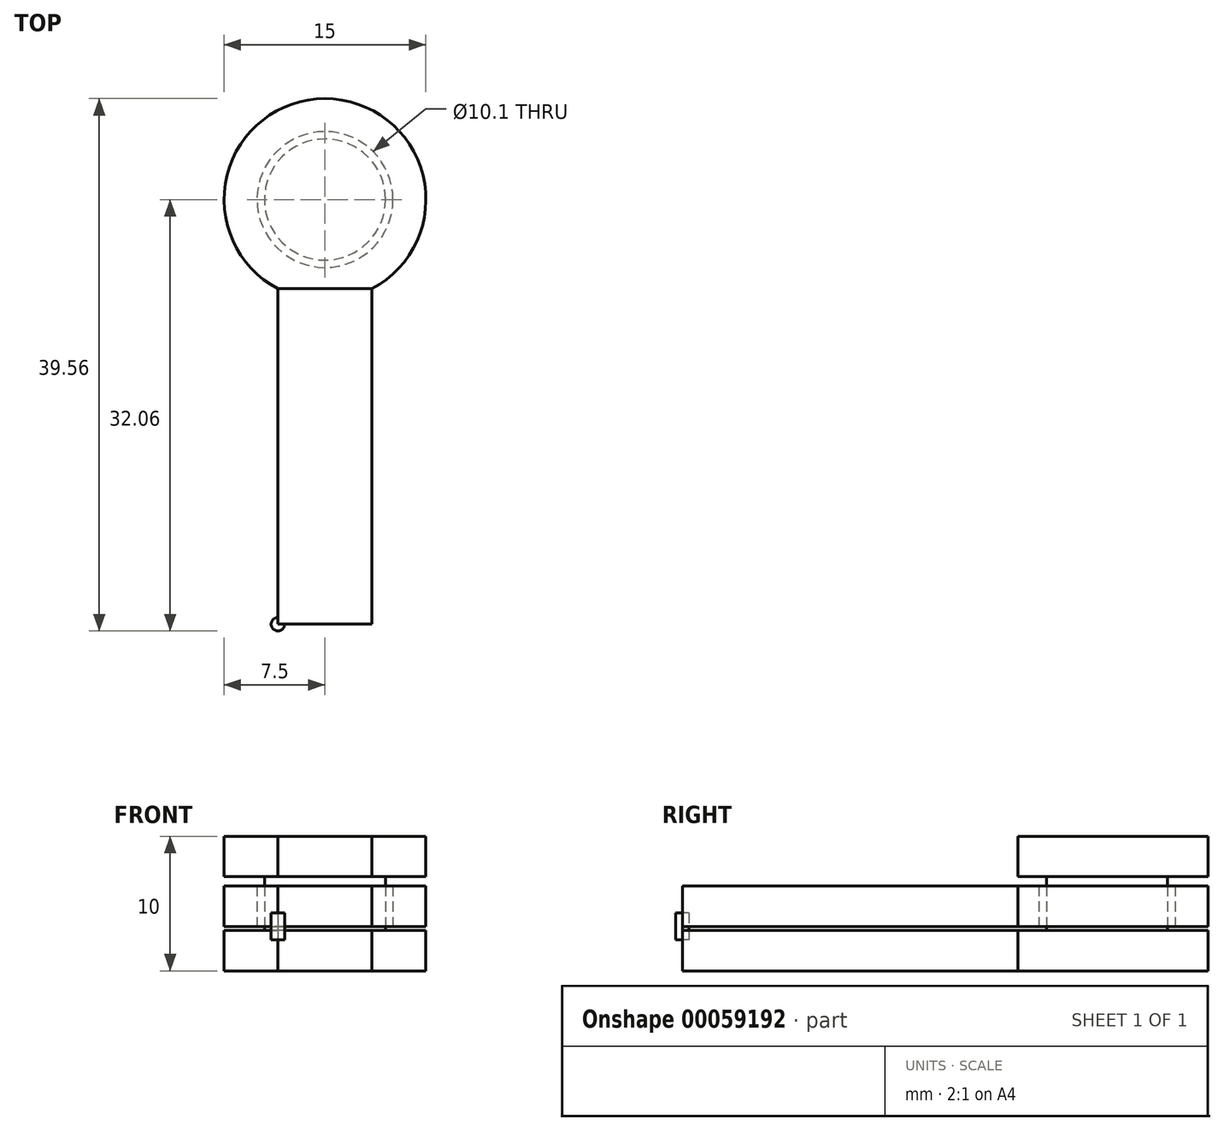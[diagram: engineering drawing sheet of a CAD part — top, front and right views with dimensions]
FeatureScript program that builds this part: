
annotation { "Feature Type Name" : "Feature", "Feature Type Description" : "" }
export const myFeature = defineFeature(function(context is Context, id is Id, definition is map)
    precondition{}
    {
        {
            var Q0;
            Q0=qCreatedBy(makeId("Top.planeOp"),FACE);
            var sketch = newSketch(context, id + "F0", { "sketchPlane" : qUnion([Q0])});
            skCircle(sketch, "E0", {"center": v(0, 0) * mm, "radius": 4.5 * mm});
            skArc(sketch, "E1", {"start": v(3.5, -6.63) * mm, "mid": v(0, 7.5) * mm, "end": v(-3.5, -6.63) * mm});
            skLineSegment(sketch, "E2.rect.bottom", {"start": v(3.5, -31.56) * mm, "end": v(-3.5, -31.56) * mm});
            skLineSegment(sketch, "E2.rect.top", {"start": v(3.5, -5.52) * mm, "end": v(-3.5, -5.52) * mm});
            skLineSegment(sketch, "E2.rect.left", {"start": v(3.5, -31.56) * mm, "end": v(3.5, -5.52) * mm});
            skLineSegment(sketch, "E2.rect.right", {"start": v(-3.5, -31.56) * mm, "end": v(-3.5, -5.52) * mm});
            skPoint(sketch, "E2.rect.middle", {"position": v(0, -18.54) * mm});
            skSolve(sketch);
        }
        {
            var Q0;
            Q0=qCreatedBy(makeId("Top.planeOp"),FACE);
            cPlane(context, id + "F1", {"entities" : qUnion([Q0]), "cplaneType" : CPlaneType.OFFSET, "offset" : 3.3 * mm, "width" : 150 * mm, "height" : 150 * mm});
        }
        {
            var Q0;
            Q0=qCreatedBy(id+"F1.planeOp",FACE);
            var sketch = newSketch(context, id + "F2", { "sketchPlane" : qUnion([Q0])});
            skLineSegment(sketch, "E3.0.0", {"start": v(3.5, -5.52) * mm, "end": v(3.5, -6.63) * mm});
            skArc(sketch, "E3.0.1", {"start": v(3.5, -6.63) * mm, "mid": v(0, 7.5) * mm, "end": v(-3.5, -6.63) * mm});
            skLineSegment(sketch, "E3.0.2", {"start": v(-3.5, -6.63) * mm, "end": v(-3.5, -5.52) * mm});
            skLineSegment(sketch, "E3.0.3", {"start": v(-3.5, -5.52) * mm, "end": v(3.5, -5.52) * mm});
            skLineSegment(sketch, "E4.0.0", {"start": v(-3.5, -31.56) * mm, "end": v(3.5, -31.56) * mm});
            skLineSegment(sketch, "E4.0.1", {"start": v(3.5, -31.56) * mm, "end": v(3.5, -6.63) * mm});
            skLineSegment(sketch, "E4.0.2", {"start": v(3.5, -6.63) * mm, "end": v(3.5, -5.52) * mm});
            skLineSegment(sketch, "E4.0.3", {"start": v(3.5, -5.52) * mm, "end": v(-3.5, -5.52) * mm});
            skLineSegment(sketch, "E4.0.4", {"start": v(-3.5, -5.52) * mm, "end": v(-3.5, -6.63) * mm});
            skLineSegment(sketch, "E4.0.5", {"start": v(-3.5, -6.63) * mm, "end": v(-3.5, -31.56) * mm});
            skCircle(sketch, "E5", {"center": v(0, 0) * mm, "radius": 5.05 * mm});
            skCircle(sketch, "E6", {"center": v(-3.5, -31.56) * mm, "radius": 0.5 * mm});
            skSolve(sketch);
        }
        {
            var Q0;
            Q0=makeQuery(id+"F2.imprint","IMPRINT",FACE,{"disambiguationData":[TD([[makeQuery(id+"F2.imprint","IMPRINT",EDGE,{"derivedFrom":sQuery(id+"F2.wireOp",EDGE,"E4.0.0")}),1.0]])]});
            var Q1;
            Q1=makeQuery(id+"F2.imprint","IMPRINT",FACE,{"disambiguationData":[TD([[makeQuery(id+"F2.imprint","IMPRINT",EDGE,{"derivedFrom":sQuery(id+"F2.wireOp",EDGE,"E3.0.1")}),1.0]])]});
            var Q2;
            {var subQ5=sQuery(id+"F2.wireOp",EDGE,"E4.0.1");Q2=makeQuery(id+"F2.imprint","IMPRINT",FACE,{"disambiguationData":[TD([[makeQuery(id+"F2.imprint","IMPRINT",EDGE,{"derivedFrom":subQ5}),1.0]])]});}
            extrude(context, id + "F3", {"entities" : qUnion([Q0, Q1, Q2]), "depth" : 3 * mm});
        }
        {
            var Q0;
            {var subQ4=sQuery(id+"F0.wireOp",EDGE,"E2.rect.bottom");Q0=makeQuery(id+"F0.imprint","IMPRINT",FACE,{"disambiguationData":[TD([[makeQuery(id+"F0.imprint","IMPRINT",EDGE,{"derivedFrom":subQ4}),-1.0]])]});}
            var Q1;
            Q1=makeQuery(id+"F0.imprint","IMPRINT",FACE,{"disambiguationData":[TD([[makeQuery(id+"F0.imprint","IMPRINT",EDGE,{"derivedFrom":sQuery(id+"F0.wireOp",EDGE,"E0")}),-1.0]])]});
            var Q2;
            Q2=makeQuery(id+"F0.imprint","IMPRINT",FACE,{"disambiguationData":[TD([[makeQuery(id+"F0.imprint","IMPRINT",EDGE,{"derivedFrom":sQuery(id+"F0.wireOp",EDGE,"E0")}),1.0]])]});
            extrude(context, id + "F4", {"entities" : qUnion([Q0, Q1, Q2]), "depth" : 3 * mm});
        }
        {
            var Q0;
            Q0=makeQuery(id+"F0.imprint","IMPRINT",FACE,{"disambiguationData":[TD([[makeQuery(id+"F0.imprint","IMPRINT",EDGE,{"derivedFrom":sQuery(id+"F0.wireOp",EDGE,"E0")}),1.0]])]});
            extrude(context, id + "F5", {"entities" : qUnion([Q0]), "operationType" : NewBodyOperationType.ADD, "depth" : 7 * mm});
        }
        {
            var Q0;
            Q0=makeQuery(id+"F5.opExtrude","CAP_FACE",FACE,{"disambiguationData":[OSD([sQuery(id+"F0.wireOp",EDGE,"E0")])],"isStart":false});
            cPlane(context, id + "F6", {"entities" : qUnion([Q0]), "cplaneType" : CPlaneType.OFFSET, "offset" : 0 * mm, "width" : 150 * mm, "height" : 150 * mm});
        }
        {
            var Q0;
            Q0=qCreatedBy(id+"F6.planeOp",FACE);
            var sketch = newSketch(context, id + "F7", { "sketchPlane" : qUnion([Q0])});
            skArc(sketch, "E7.0", {"start": v(3.5, -6.63) * mm, "mid": v(0, 7.5) * mm, "end": v(-3.5, -6.63) * mm});
            skLineSegment(sketch, "E8", {"start": v(-3.5, -6.63) * mm, "end": v(3.5, -6.63) * mm});
            skSolve(sketch);
        }
        {
            var Q0;
            Q0 = qSketchRegion(id + "F7", true);
            extrude(context, id + "F8", {"entities" : qUnion([Q0]), "operationType" : NewBodyOperationType.ADD, "depth" : 3 * mm});
        }
        {
            var Q0;
            {var subQ0=sQuery(id+"F2.wireOp",EDGE,"E4.0.5");var subQ1=sQuery(id+"F2.wireOp",EDGE,"E4.0.0");var subQ2=makeQuery(id+"F2.imprint","INTERSECT",VERTEX,{"derivedFrom":[subQ1,subQ0]});Q0=makeQuery(id+"F2.imprint","IMPRINT",FACE,{"disambiguationData":[TD([[makeQuery(id+"F2.imprint","IMPRINT",EDGE,{"disambiguationData":[TD([[subQ2,-1.0]])],"derivedFrom":subQ1}),-1.0]])]});}
            extrude(context, id + "F9", {"entities" : qUnion([Q0]), "operationType" : NewBodyOperationType.ADD, "depth" : 1 * mm, "hasSecondDirection" : true, "secondDirectionOppositeDirection" : true, "secondDirectionDepth" : 1 * mm});
        }
    });
